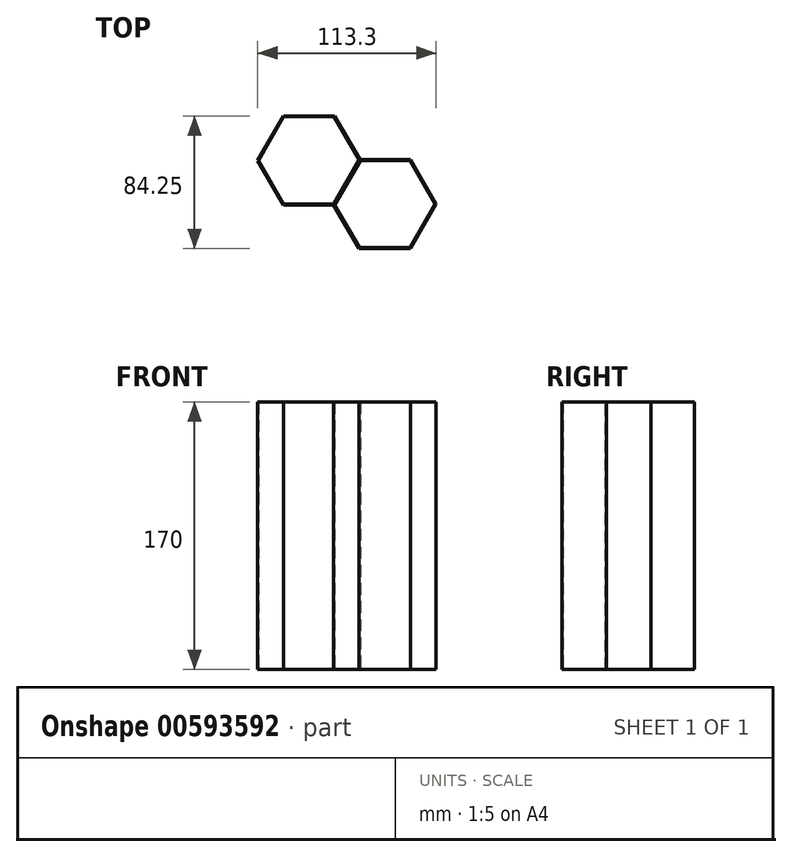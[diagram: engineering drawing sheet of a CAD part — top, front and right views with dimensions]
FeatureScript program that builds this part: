
annotation { "Feature Type Name" : "Feature", "Feature Type Description" : "" }
export const myFeature = defineFeature(function(context is Context, id is Id, definition is map)
    precondition{}
    {
        {
            var Q0;
            Q0=qCreatedBy(makeId("Top.planeOp"),FACE);
            var sketch = newSketch(context, id + "F0", { "sketchPlane" : qUnion([Q0])});
            skCircle(sketch, "E0.cCircle", {"center": v(0, 0) * mm, "radius": 28.25 * mm, "construction": true});
            skLineSegment(sketch, "E0.0", {"start": v(-16.31, 28.25) * mm, "end": v(16.31, 28.25) * mm});
            skLineSegment(sketch, "E0.1", {"start": v(16.31, 28.25) * mm, "end": v(32.62, 0) * mm});
            skLineSegment(sketch, "E0.2", {"start": v(32.62, 0) * mm, "end": v(16.31, -28.25) * mm});
            skLineSegment(sketch, "E0.3", {"start": v(16.31, -28.25) * mm, "end": v(-16.31, -28.25) * mm});
            skLineSegment(sketch, "E0.4", {"start": v(-16.31, -28.25) * mm, "end": v(-32.62, 0) * mm});
            skLineSegment(sketch, "E0.5", {"start": v(-32.62, 0) * mm, "end": v(-16.31, 28.25) * mm});
            skPoint(sketch, "E0.0.midPoint", {"position": v(0, 28.25) * mm});
            skSolve(sketch);
        }
        {
            var Q0;
            Q0=makeQuery(id+"F0.imprint","IMPRINT",FACE,{"disambiguationData":[TD([[makeQuery(id+"F0.imprint","IMPRINT",EDGE,{"derivedFrom":sQuery(id+"F0.wireOp",EDGE,"625dc4df-1560-4c75-8085-82a92da362ae.0")}),-1.0]])]});
            var Q1;
            Q1=makeQuery(id+"F0.imprint","IMPRINT",FACE,{"disambiguationData":[TD([[makeQuery(id+"F0.imprint","IMPRINT",EDGE,{"derivedFrom":sQuery(id+"F0.wireOp",EDGE,"625dc4df-1560-4c75-8085-82a92da362ae.5")}),1.0]])]});
            var Q2;
            Q2=makeQuery(id+"F0.imprint","IMPRINT",FACE,{"disambiguationData":[TD([[makeQuery(id+"F0.imprint","IMPRINT",EDGE,{"derivedFrom":sQuery(id+"F0.wireOp",EDGE,"625dc4df-1560-4c75-8085-82a92da362ae.0")}),1.0]])]});
            var Q3;
            Q3=makeQuery(id+"F0.imprint","IMPRINT",FACE,{"disambiguationData":[TD([[makeQuery(id+"F0.imprint","IMPRINT",EDGE,{"derivedFrom":sQuery(id+"F0.wireOp",EDGE,"625dc4df-1560-4c75-8085-82a92da362ae.3")}),1.0]])]});
            var Q4;
            Q4=makeQuery(id+"F0.imprint","IMPRINT",FACE,{"disambiguationData":[TD([[makeQuery(id+"F0.imprint","IMPRINT",EDGE,{"derivedFrom":sQuery(id+"F0.wireOp",EDGE,"625dc4df-1560-4c75-8085-82a92da362ae.2")}),1.0]])]});
            var Q5;
            Q5=makeQuery(id+"F0.imprint","IMPRINT",FACE,{"disambiguationData":[TD([[makeQuery(id+"F0.imprint","IMPRINT",EDGE,{"derivedFrom":sQuery(id+"F0.wireOp",EDGE,"E0.0")}),-1.0]])]});
            extrude(context, id + "F1", {"entities" : qUnion([Q0, Q1, Q2, Q3, Q4, Q5]), "depth" : 170 * mm, "offsetDistance" : 25 * mm});
        }
        {
            var Q0;
            Q0=makeQuery(id+"F1.opExtrude","CAP_FACE",FACE,{"disambiguationData":[OSD([sQuery(id+"F0.wireOp",EDGE,"E0.0"),sQuery(id+"F0.wireOp",EDGE,"E0.1"),sQuery(id+"F0.wireOp",EDGE,"E0.2"),sQuery(id+"F0.wireOp",EDGE,"E0.3"),sQuery(id+"F0.wireOp",EDGE,"E0.4"),sQuery(id+"F0.wireOp",EDGE,"E0.5")])],"isStart":false});
            shell(context, id + "F2", {"entities" : qUnion([Q0]), "thickness" : 0.5 * mm});
        }
        {
            var Q0;
            Q0=makeQuery(id+"F1.opExtrude","SWEPT_BODY",BODY,{"disambiguationData":[OSD([sQuery(id+"F0.wireOp",EDGE,"E0.0"),sQuery(id+"F0.wireOp",EDGE,"E0.1"),sQuery(id+"F0.wireOp",EDGE,"E0.2"),sQuery(id+"F0.wireOp",EDGE,"E0.3"),sQuery(id+"F0.wireOp",EDGE,"E0.4"),sQuery(id+"F0.wireOp",EDGE,"E0.5")])]});
            var Q1;
            Q1=makeQuery(id+"F2.opShell","OFFSET_FACE",FACE,{"disambiguationData":[OSD([sQuery(id+"F0.wireOp",EDGE,"E0.5")])]});
            mirror(context, id + "F3", {"operationType" : NewBodyOperationType.ADD, "entities" : qUnion([Q0]), "mirrorPlane" : qUnion([Q1])});
        }
    });
